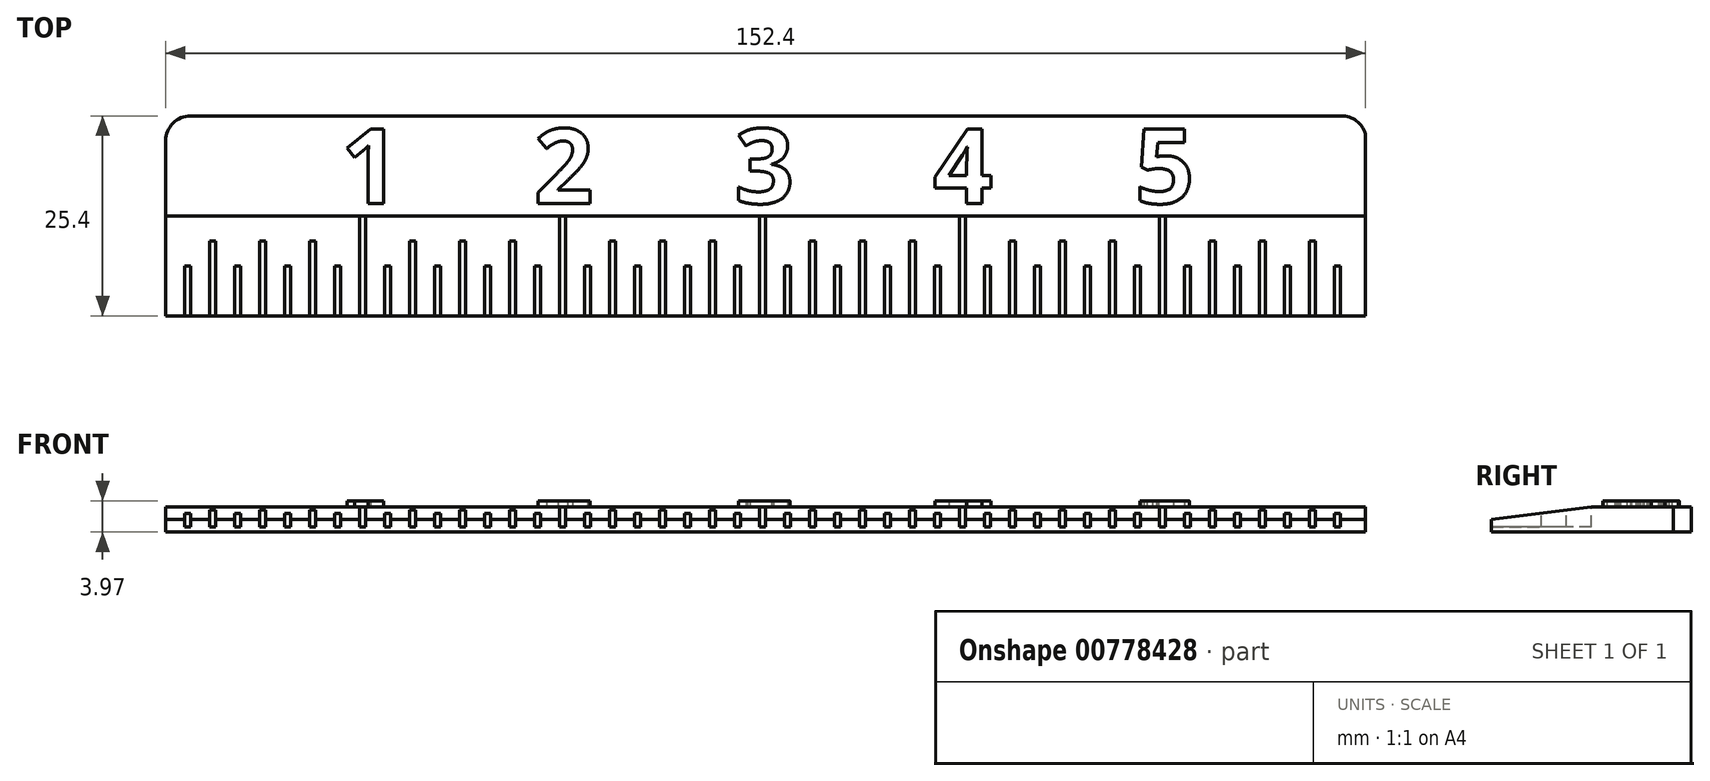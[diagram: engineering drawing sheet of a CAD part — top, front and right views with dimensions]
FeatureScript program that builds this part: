
annotation { "Feature Type Name" : "Feature", "Feature Type Description" : "" }
export const myFeature = defineFeature(function(context is Context, id is Id, definition is map)
    precondition{}
    {
        {
            var Q0;
            Q0=qCreatedBy(makeId("Top.planeOp"),FACE);
            var sketch = newSketch(context, id + "F0", { "sketchPlane" : qUnion([Q0])});
            skLineSegment(sketch, "E0.bottom", {"start": v(-76.26, 7.66) * mm, "end": v(76.14, 7.66) * mm});
            skLineSegment(sketch, "E0.top", {"start": v(-76.26, -17.74) * mm, "end": v(76.14, -17.74) * mm});
            skLineSegment(sketch, "E0.left", {"start": v(-76.26, 7.66) * mm, "end": v(-76.26, -17.74) * mm});
            skLineSegment(sketch, "E0.right", {"start": v(76.14, 7.66) * mm, "end": v(76.14, -17.74) * mm});
            skSolve(sketch);
        }
        {
            var Q0;
            Q0 = qSketchRegion(id + "F0", true);
            extrude(context, id + "F1", {"entities" : qUnion([Q0]), "depth" : 3.17 * mm, "offsetDistance" : 25.4 * mm});
        }
        {
            var Q0;
            Q0=makeQuery(id+"F1.opExtrude","CAP_FACE",FACE,{"disambiguationData":[OSD([sQuery(id+"F0.wireOp",EDGE,"E0.bottom"),sQuery(id+"F0.wireOp",EDGE,"E0.top"),sQuery(id+"F0.wireOp",EDGE,"E0.left"),sQuery(id+"F0.wireOp",EDGE,"E0.right")])],"isStart":false});
            var sketch = newSketch(context, id + "F2", { "sketchPlane" : qUnion([Q0])});
            skPoint(sketch, "E1.firstSnap0", {"position": v(-76.26, -5.04) * mm});
            skLineSegment(sketch, "E1.bottom", {"start": v(-51.66, -5.04) * mm, "end": v(-50.86, -5.04) * mm});
            skLineSegment(sketch, "E1.top", {"start": v(-51.66, -17.74) * mm, "end": v(-50.86, -17.74) * mm});
            skLineSegment(sketch, "E1.left", {"start": v(-51.66, -5.04) * mm, "end": v(-51.66, -17.74) * mm});
            skLineSegment(sketch, "E1.right", {"start": v(-50.86, -5.04) * mm, "end": v(-50.86, -17.74) * mm});
            skLineSegment(sketch, "E2.1.0.0", {"start": v(-26.26, -5.04) * mm, "end": v(-25.46, -5.04) * mm});
            skLineSegment(sketch, "E2.1.0.1", {"start": v(-26.26, -5.04) * mm, "end": v(-26.26, -17.74) * mm});
            skLineSegment(sketch, "E2.1.0.2", {"start": v(-25.46, -5.04) * mm, "end": v(-25.46, -17.74) * mm});
            skLineSegment(sketch, "E2.1.0.3", {"start": v(-26.26, -17.74) * mm, "end": v(-25.46, -17.74) * mm});
            skLineSegment(sketch, "E2.2.0.0", {"start": v(-0.86, -5.04) * mm, "end": v(-0.06, -5.04) * mm});
            skLineSegment(sketch, "E2.2.0.1", {"start": v(-0.86, -5.04) * mm, "end": v(-0.86, -17.74) * mm});
            skLineSegment(sketch, "E2.2.0.2", {"start": v(-0.06, -5.04) * mm, "end": v(-0.06, -17.74) * mm});
            skLineSegment(sketch, "E2.2.0.3", {"start": v(-0.86, -17.74) * mm, "end": v(-0.06, -17.74) * mm});
            skLineSegment(sketch, "E2.3.0.0", {"start": v(24.54, -5.04) * mm, "end": v(25.34, -5.04) * mm});
            skLineSegment(sketch, "E2.3.0.1", {"start": v(24.54, -5.04) * mm, "end": v(24.54, -17.74) * mm});
            skLineSegment(sketch, "E2.3.0.2", {"start": v(25.34, -5.04) * mm, "end": v(25.34, -17.74) * mm});
            skLineSegment(sketch, "E2.3.0.3", {"start": v(24.54, -17.74) * mm, "end": v(25.34, -17.74) * mm});
            skLineSegment(sketch, "E2.4.0.0", {"start": v(49.94, -5.04) * mm, "end": v(50.74, -5.04) * mm});
            skLineSegment(sketch, "E2.4.0.1", {"start": v(49.94, -5.04) * mm, "end": v(49.94, -17.74) * mm});
            skLineSegment(sketch, "E2.4.0.2", {"start": v(50.74, -5.04) * mm, "end": v(50.74, -17.74) * mm});
            skLineSegment(sketch, "E2.4.0.3", {"start": v(49.94, -17.74) * mm, "end": v(50.74, -17.74) * mm});
            skLineSegment(sketch, "E2.direction1", {"start": v(-51.66, -17.74) * mm, "end": v(-26.26, -17.74) * mm, "construction": true});
            skSolve(sketch);
        }
        {
            var Q0;
            Q0 = qSketchRegion(id + "F2", true);
            extrude(context, id + "F3", {"entities" : qUnion([Q0]), "operationType" : NewBodyOperationType.REMOVE, "oppositeDirection" : true, "depth" : 2.54 * mm, "offsetDistance" : 25.4 * mm});
        }
        {
            var Q0;
            Q0=makeQuery(id+"F1.opExtrude","CAP_FACE",FACE,{"disambiguationData":[OSD([sQuery(id+"F0.wireOp",EDGE,"E0.bottom"),sQuery(id+"F0.wireOp",EDGE,"E0.top"),sQuery(id+"F0.wireOp",EDGE,"E0.left"),sQuery(id+"F0.wireOp",EDGE,"E0.right")])],"isStart":false});
            var sketch = newSketch(context, id + "F4", { "sketchPlane" : qUnion([Q0])});
            skLineSegment(sketch, "E3.bottom", {"start": v(-70.7, -8.21) * mm, "end": v(-69.91, -8.21) * mm});
            skLineSegment(sketch, "E3.top", {"start": v(-70.7, -17.74) * mm, "end": v(-69.91, -17.74) * mm});
            skLineSegment(sketch, "E3.left", {"start": v(-70.7, -8.21) * mm, "end": v(-70.7, -17.74) * mm});
            skLineSegment(sketch, "E3.right", {"start": v(-69.91, -8.21) * mm, "end": v(-69.91, -17.74) * mm});
            skLineSegment(sketch, "E4.1.0.0", {"start": v(-64.36, -8.21) * mm, "end": v(-64.36, -17.74) * mm});
            skLineSegment(sketch, "E4.1.0.1", {"start": v(-63.56, -8.21) * mm, "end": v(-63.56, -17.74) * mm});
            skLineSegment(sketch, "E4.1.0.2", {"start": v(-64.36, -8.21) * mm, "end": v(-63.56, -8.21) * mm});
            skLineSegment(sketch, "E4.1.0.3", {"start": v(-64.36, -17.74) * mm, "end": v(-63.56, -17.74) * mm});
            skLineSegment(sketch, "E4.2.0.0", {"start": v(-58, -8.21) * mm, "end": v(-58, -17.74) * mm});
            skLineSegment(sketch, "E4.2.0.1", {"start": v(-57.21, -8.21) * mm, "end": v(-57.21, -17.74) * mm});
            skLineSegment(sketch, "E4.2.0.2", {"start": v(-58, -8.21) * mm, "end": v(-57.21, -8.21) * mm});
            skLineSegment(sketch, "E4.2.0.3", {"start": v(-58, -17.74) * mm, "end": v(-57.21, -17.74) * mm});
            skLineSegment(sketch, "E4.direction1", {"start": v(-70.7, -17.74) * mm, "end": v(-64.36, -17.74) * mm, "construction": true});
            skLineSegment(sketch, "E5.1.0.0", {"start": v(-31.81, -8.21) * mm, "end": v(-31.81, -17.74) * mm});
            skLineSegment(sketch, "E5.1.0.1", {"start": v(-32.6, -17.74) * mm, "end": v(-31.81, -17.74) * mm});
            skLineSegment(sketch, "E5.1.0.2", {"start": v(-45.3, -17.74) * mm, "end": v(-38.96, -17.74) * mm, "construction": true});
            skLineSegment(sketch, "E5.1.0.3", {"start": v(-32.6, -8.21) * mm, "end": v(-32.6, -17.74) * mm});
            skLineSegment(sketch, "E5.1.0.4", {"start": v(-38.96, -17.74) * mm, "end": v(-38.16, -17.74) * mm});
            skLineSegment(sketch, "E5.1.0.5", {"start": v(-38.16, -8.21) * mm, "end": v(-38.16, -17.74) * mm});
            skLineSegment(sketch, "E5.1.0.6", {"start": v(-38.96, -8.21) * mm, "end": v(-38.96, -17.74) * mm});
            skLineSegment(sketch, "E5.1.0.7", {"start": v(-44.51, -8.21) * mm, "end": v(-44.51, -17.74) * mm});
            skLineSegment(sketch, "E5.1.0.8", {"start": v(-45.3, -8.21) * mm, "end": v(-45.3, -17.74) * mm});
            skLineSegment(sketch, "E5.1.0.9", {"start": v(-45.3, -17.74) * mm, "end": v(-44.51, -17.74) * mm});
            skLineSegment(sketch, "E5.1.0.10", {"start": v(-32.6, -8.21) * mm, "end": v(-31.81, -8.21) * mm});
            skLineSegment(sketch, "E5.1.0.11", {"start": v(-38.96, -8.21) * mm, "end": v(-38.16, -8.21) * mm});
            skLineSegment(sketch, "E5.1.0.12", {"start": v(-45.3, -8.21) * mm, "end": v(-44.51, -8.21) * mm});
            skLineSegment(sketch, "E5.2.0.0", {"start": v(-6.41, -8.21) * mm, "end": v(-6.41, -17.74) * mm});
            skLineSegment(sketch, "E5.2.0.1", {"start": v(-7.2, -17.74) * mm, "end": v(-6.41, -17.74) * mm});
            skLineSegment(sketch, "E5.2.0.2", {"start": v(-19.9, -17.74) * mm, "end": v(-13.56, -17.74) * mm, "construction": true});
            skLineSegment(sketch, "E5.2.0.3", {"start": v(-7.2, -8.21) * mm, "end": v(-7.2, -17.74) * mm});
            skLineSegment(sketch, "E5.2.0.4", {"start": v(-13.56, -17.74) * mm, "end": v(-12.76, -17.74) * mm});
            skLineSegment(sketch, "E5.2.0.5", {"start": v(-12.76, -8.21) * mm, "end": v(-12.76, -17.74) * mm});
            skLineSegment(sketch, "E5.2.0.6", {"start": v(-13.56, -8.21) * mm, "end": v(-13.56, -17.74) * mm});
            skLineSegment(sketch, "E5.2.0.7", {"start": v(-19.11, -8.21) * mm, "end": v(-19.11, -17.74) * mm});
            skLineSegment(sketch, "E5.2.0.8", {"start": v(-19.9, -8.21) * mm, "end": v(-19.9, -17.74) * mm});
            skLineSegment(sketch, "E5.2.0.9", {"start": v(-19.9, -17.74) * mm, "end": v(-19.11, -17.74) * mm});
            skLineSegment(sketch, "E5.2.0.10", {"start": v(-7.2, -8.21) * mm, "end": v(-6.41, -8.21) * mm});
            skLineSegment(sketch, "E5.2.0.11", {"start": v(-13.56, -8.21) * mm, "end": v(-12.76, -8.21) * mm});
            skLineSegment(sketch, "E5.2.0.12", {"start": v(-19.9, -8.21) * mm, "end": v(-19.11, -8.21) * mm});
            skLineSegment(sketch, "E5.3.0.0", {"start": v(18.99, -8.21) * mm, "end": v(18.99, -17.74) * mm});
            skLineSegment(sketch, "E5.3.0.1", {"start": v(18.2, -17.74) * mm, "end": v(18.99, -17.74) * mm});
            skLineSegment(sketch, "E5.3.0.2", {"start": v(5.5, -17.74) * mm, "end": v(11.84, -17.74) * mm, "construction": true});
            skLineSegment(sketch, "E5.3.0.3", {"start": v(18.2, -8.21) * mm, "end": v(18.2, -17.74) * mm});
            skLineSegment(sketch, "E5.3.0.4", {"start": v(11.84, -17.74) * mm, "end": v(12.64, -17.74) * mm});
            skLineSegment(sketch, "E5.3.0.5", {"start": v(12.64, -8.21) * mm, "end": v(12.64, -17.74) * mm});
            skLineSegment(sketch, "E5.3.0.6", {"start": v(11.84, -8.21) * mm, "end": v(11.84, -17.74) * mm});
            skLineSegment(sketch, "E5.3.0.7", {"start": v(6.29, -8.21) * mm, "end": v(6.29, -17.74) * mm});
            skLineSegment(sketch, "E5.3.0.8", {"start": v(5.5, -8.21) * mm, "end": v(5.5, -17.74) * mm});
            skLineSegment(sketch, "E5.3.0.9", {"start": v(5.5, -17.74) * mm, "end": v(6.29, -17.74) * mm});
            skLineSegment(sketch, "E5.3.0.10", {"start": v(18.2, -8.21) * mm, "end": v(18.99, -8.21) * mm});
            skLineSegment(sketch, "E5.3.0.11", {"start": v(11.84, -8.21) * mm, "end": v(12.64, -8.21) * mm});
            skLineSegment(sketch, "E5.3.0.12", {"start": v(5.5, -8.21) * mm, "end": v(6.29, -8.21) * mm});
            skLineSegment(sketch, "E5.4.0.0", {"start": v(44.39, -8.21) * mm, "end": v(44.39, -17.74) * mm});
            skLineSegment(sketch, "E5.4.0.1", {"start": v(43.6, -17.74) * mm, "end": v(44.39, -17.74) * mm});
            skLineSegment(sketch, "E5.4.0.2", {"start": v(30.9, -17.74) * mm, "end": v(37.24, -17.74) * mm, "construction": true});
            skLineSegment(sketch, "E5.4.0.3", {"start": v(43.6, -8.21) * mm, "end": v(43.6, -17.74) * mm});
            skLineSegment(sketch, "E5.4.0.4", {"start": v(37.24, -17.74) * mm, "end": v(38.04, -17.74) * mm});
            skLineSegment(sketch, "E5.4.0.5", {"start": v(38.04, -8.21) * mm, "end": v(38.04, -17.74) * mm});
            skLineSegment(sketch, "E5.4.0.6", {"start": v(37.24, -8.21) * mm, "end": v(37.24, -17.74) * mm});
            skLineSegment(sketch, "E5.4.0.7", {"start": v(31.69, -8.21) * mm, "end": v(31.69, -17.74) * mm});
            skLineSegment(sketch, "E5.4.0.8", {"start": v(30.9, -8.21) * mm, "end": v(30.9, -17.74) * mm});
            skLineSegment(sketch, "E5.4.0.9", {"start": v(30.9, -17.74) * mm, "end": v(31.69, -17.74) * mm});
            skLineSegment(sketch, "E5.4.0.10", {"start": v(43.6, -8.21) * mm, "end": v(44.39, -8.21) * mm});
            skLineSegment(sketch, "E5.4.0.11", {"start": v(37.24, -8.21) * mm, "end": v(38.04, -8.21) * mm});
            skLineSegment(sketch, "E5.4.0.12", {"start": v(30.9, -8.21) * mm, "end": v(31.69, -8.21) * mm});
            skLineSegment(sketch, "E5.5.0.0", {"start": v(69.79, -8.21) * mm, "end": v(69.79, -17.74) * mm});
            skLineSegment(sketch, "E5.5.0.1", {"start": v(69, -17.74) * mm, "end": v(69.79, -17.74) * mm});
            skLineSegment(sketch, "E5.5.0.2", {"start": v(56.3, -17.74) * mm, "end": v(62.64, -17.74) * mm, "construction": true});
            skLineSegment(sketch, "E5.5.0.3", {"start": v(69, -8.21) * mm, "end": v(69, -17.74) * mm});
            skLineSegment(sketch, "E5.5.0.4", {"start": v(62.64, -17.74) * mm, "end": v(63.44, -17.74) * mm});
            skLineSegment(sketch, "E5.5.0.5", {"start": v(63.44, -8.21) * mm, "end": v(63.44, -17.74) * mm});
            skLineSegment(sketch, "E5.5.0.6", {"start": v(62.64, -8.21) * mm, "end": v(62.64, -17.74) * mm});
            skLineSegment(sketch, "E5.5.0.7", {"start": v(57.09, -8.21) * mm, "end": v(57.09, -17.74) * mm});
            skLineSegment(sketch, "E5.5.0.8", {"start": v(56.3, -8.21) * mm, "end": v(56.3, -17.74) * mm});
            skLineSegment(sketch, "E5.5.0.9", {"start": v(56.3, -17.74) * mm, "end": v(57.09, -17.74) * mm});
            skLineSegment(sketch, "E5.5.0.10", {"start": v(69, -8.21) * mm, "end": v(69.79, -8.21) * mm});
            skLineSegment(sketch, "E5.5.0.11", {"start": v(62.64, -8.21) * mm, "end": v(63.44, -8.21) * mm});
            skLineSegment(sketch, "E5.5.0.12", {"start": v(56.3, -8.21) * mm, "end": v(57.09, -8.21) * mm});
            skLineSegment(sketch, "E5.direction1", {"start": v(-70.7, -17.74) * mm, "end": v(-45.3, -17.74) * mm, "construction": true});
            skSolve(sketch);
        }
        {
            var Q0;
            Q0 = qSketchRegion(id + "F4", true);
            extrude(context, id + "F5", {"entities" : qUnion([Q0]), "operationType" : NewBodyOperationType.REMOVE, "oppositeDirection" : true, "depth" : 2.54 * mm, "offsetDistance" : 25.4 * mm});
        }
        {
            var Q0;
            Q0=makeQuery(id+"F1.opExtrude","CAP_FACE",FACE,{"disambiguationData":[OSD([sQuery(id+"F0.wireOp",EDGE,"E0.bottom"),sQuery(id+"F0.wireOp",EDGE,"E0.top"),sQuery(id+"F0.wireOp",EDGE,"E0.left"),sQuery(id+"F0.wireOp",EDGE,"E0.right")])],"isStart":false});
            var sketch = newSketch(context, id + "F6", { "sketchPlane" : qUnion([Q0])});
            skLineSegment(sketch, "E6.bottom", {"start": v(-73.88, -17.74) * mm, "end": v(-73.09, -17.74) * mm});
            skLineSegment(sketch, "E6.top", {"start": v(-73.88, -11.39) * mm, "end": v(-73.09, -11.39) * mm});
            skLineSegment(sketch, "E6.left", {"start": v(-73.88, -17.74) * mm, "end": v(-73.88, -11.39) * mm});
            skLineSegment(sketch, "E6.right", {"start": v(-73.09, -17.74) * mm, "end": v(-73.09, -11.39) * mm});
            skLineSegment(sketch, "E7.1.0.0", {"start": v(-67.53, -17.74) * mm, "end": v(-66.74, -17.74) * mm});
            skLineSegment(sketch, "E7.1.0.1", {"start": v(-67.53, -11.39) * mm, "end": v(-66.74, -11.39) * mm});
            skLineSegment(sketch, "E7.1.0.2", {"start": v(-67.53, -17.74) * mm, "end": v(-67.53, -11.39) * mm});
            skLineSegment(sketch, "E7.1.0.3", {"start": v(-66.74, -17.74) * mm, "end": v(-66.74, -11.39) * mm});
            skLineSegment(sketch, "E7.2.0.0", {"start": v(-61.18, -17.74) * mm, "end": v(-60.39, -17.74) * mm});
            skLineSegment(sketch, "E7.2.0.1", {"start": v(-61.18, -11.39) * mm, "end": v(-60.39, -11.39) * mm});
            skLineSegment(sketch, "E7.2.0.2", {"start": v(-61.18, -17.74) * mm, "end": v(-61.18, -11.39) * mm});
            skLineSegment(sketch, "E7.2.0.3", {"start": v(-60.39, -17.74) * mm, "end": v(-60.39, -11.39) * mm});
            skLineSegment(sketch, "E7.3.0.0", {"start": v(-54.83, -17.74) * mm, "end": v(-54.04, -17.74) * mm});
            skLineSegment(sketch, "E7.3.0.1", {"start": v(-54.83, -11.39) * mm, "end": v(-54.04, -11.39) * mm});
            skLineSegment(sketch, "E7.3.0.2", {"start": v(-54.83, -17.74) * mm, "end": v(-54.83, -11.39) * mm});
            skLineSegment(sketch, "E7.3.0.3", {"start": v(-54.04, -17.74) * mm, "end": v(-54.04, -11.39) * mm});
            skLineSegment(sketch, "E7.direction1", {"start": v(-73.88, -17.74) * mm, "end": v(-67.53, -17.74) * mm, "construction": true});
            skLineSegment(sketch, "E8.1.0.0", {"start": v(-29.43, -17.74) * mm, "end": v(-28.64, -17.74) * mm});
            skLineSegment(sketch, "E8.1.0.1", {"start": v(-34.99, -17.74) * mm, "end": v(-34.99, -11.39) * mm});
            skLineSegment(sketch, "E8.1.0.2", {"start": v(-35.78, -17.74) * mm, "end": v(-35.78, -11.39) * mm});
            skLineSegment(sketch, "E8.1.0.3", {"start": v(-48.48, -17.74) * mm, "end": v(-42.13, -17.74) * mm, "construction": true});
            skLineSegment(sketch, "E8.1.0.4", {"start": v(-35.78, -11.39) * mm, "end": v(-34.99, -11.39) * mm});
            skLineSegment(sketch, "E8.1.0.5", {"start": v(-35.78, -17.74) * mm, "end": v(-34.99, -17.74) * mm});
            skLineSegment(sketch, "E8.1.0.6", {"start": v(-29.43, -11.39) * mm, "end": v(-28.64, -11.39) * mm});
            skLineSegment(sketch, "E8.1.0.7", {"start": v(-29.43, -17.74) * mm, "end": v(-29.43, -11.39) * mm});
            skLineSegment(sketch, "E8.1.0.8", {"start": v(-28.64, -17.74) * mm, "end": v(-28.64, -11.39) * mm});
            skLineSegment(sketch, "E8.1.0.9", {"start": v(-48.48, -11.39) * mm, "end": v(-47.69, -11.39) * mm});
            skLineSegment(sketch, "E8.1.0.10", {"start": v(-48.48, -17.74) * mm, "end": v(-48.48, -11.39) * mm});
            skLineSegment(sketch, "E8.1.0.11", {"start": v(-47.69, -17.74) * mm, "end": v(-47.69, -11.39) * mm});
            skLineSegment(sketch, "E8.1.0.12", {"start": v(-42.13, -17.74) * mm, "end": v(-41.34, -17.74) * mm});
            skLineSegment(sketch, "E8.1.0.13", {"start": v(-42.13, -11.39) * mm, "end": v(-41.34, -11.39) * mm});
            skLineSegment(sketch, "E8.1.0.14", {"start": v(-42.13, -17.74) * mm, "end": v(-42.13, -11.39) * mm});
            skLineSegment(sketch, "E8.1.0.15", {"start": v(-41.34, -17.74) * mm, "end": v(-41.34, -11.39) * mm});
            skLineSegment(sketch, "E8.1.0.16", {"start": v(-48.48, -17.74) * mm, "end": v(-47.69, -17.74) * mm});
            skLineSegment(sketch, "E8.2.0.0", {"start": v(-4.03, -17.74) * mm, "end": v(-3.24, -17.74) * mm});
            skLineSegment(sketch, "E8.2.0.1", {"start": v(-9.59, -17.74) * mm, "end": v(-9.59, -11.39) * mm});
            skLineSegment(sketch, "E8.2.0.2", {"start": v(-10.38, -17.74) * mm, "end": v(-10.38, -11.39) * mm});
            skLineSegment(sketch, "E8.2.0.3", {"start": v(-23.08, -17.74) * mm, "end": v(-16.73, -17.74) * mm, "construction": true});
            skLineSegment(sketch, "E8.2.0.4", {"start": v(-10.38, -11.39) * mm, "end": v(-9.59, -11.39) * mm});
            skLineSegment(sketch, "E8.2.0.5", {"start": v(-10.38, -17.74) * mm, "end": v(-9.59, -17.74) * mm});
            skLineSegment(sketch, "E8.2.0.6", {"start": v(-4.03, -11.39) * mm, "end": v(-3.24, -11.39) * mm});
            skLineSegment(sketch, "E8.2.0.7", {"start": v(-4.03, -17.74) * mm, "end": v(-4.03, -11.39) * mm});
            skLineSegment(sketch, "E8.2.0.8", {"start": v(-3.24, -17.74) * mm, "end": v(-3.24, -11.39) * mm});
            skLineSegment(sketch, "E8.2.0.9", {"start": v(-23.08, -11.39) * mm, "end": v(-22.29, -11.39) * mm});
            skLineSegment(sketch, "E8.2.0.10", {"start": v(-23.08, -17.74) * mm, "end": v(-23.08, -11.39) * mm});
            skLineSegment(sketch, "E8.2.0.11", {"start": v(-22.29, -17.74) * mm, "end": v(-22.29, -11.39) * mm});
            skLineSegment(sketch, "E8.2.0.12", {"start": v(-16.73, -17.74) * mm, "end": v(-15.94, -17.74) * mm});
            skLineSegment(sketch, "E8.2.0.13", {"start": v(-16.73, -11.39) * mm, "end": v(-15.94, -11.39) * mm});
            skLineSegment(sketch, "E8.2.0.14", {"start": v(-16.73, -17.74) * mm, "end": v(-16.73, -11.39) * mm});
            skLineSegment(sketch, "E8.2.0.15", {"start": v(-15.94, -17.74) * mm, "end": v(-15.94, -11.39) * mm});
            skLineSegment(sketch, "E8.2.0.16", {"start": v(-23.08, -17.74) * mm, "end": v(-22.29, -17.74) * mm});
            skLineSegment(sketch, "E8.3.0.0", {"start": v(21.37, -17.74) * mm, "end": v(22.16, -17.74) * mm});
            skLineSegment(sketch, "E8.3.0.1", {"start": v(15.81, -17.74) * mm, "end": v(15.81, -11.39) * mm});
            skLineSegment(sketch, "E8.3.0.2", {"start": v(15.02, -17.74) * mm, "end": v(15.02, -11.39) * mm});
            skLineSegment(sketch, "E8.3.0.3", {"start": v(2.32, -17.74) * mm, "end": v(8.67, -17.74) * mm, "construction": true});
            skLineSegment(sketch, "E8.3.0.4", {"start": v(15.02, -11.39) * mm, "end": v(15.81, -11.39) * mm});
            skLineSegment(sketch, "E8.3.0.5", {"start": v(15.02, -17.74) * mm, "end": v(15.81, -17.74) * mm});
            skLineSegment(sketch, "E8.3.0.6", {"start": v(21.37, -11.39) * mm, "end": v(22.16, -11.39) * mm});
            skLineSegment(sketch, "E8.3.0.7", {"start": v(21.37, -17.74) * mm, "end": v(21.37, -11.39) * mm});
            skLineSegment(sketch, "E8.3.0.8", {"start": v(22.16, -17.74) * mm, "end": v(22.16, -11.39) * mm});
            skLineSegment(sketch, "E8.3.0.9", {"start": v(2.32, -11.39) * mm, "end": v(3.11, -11.39) * mm});
            skLineSegment(sketch, "E8.3.0.10", {"start": v(2.32, -17.74) * mm, "end": v(2.32, -11.39) * mm});
            skLineSegment(sketch, "E8.3.0.11", {"start": v(3.11, -17.74) * mm, "end": v(3.11, -11.39) * mm});
            skLineSegment(sketch, "E8.3.0.12", {"start": v(8.67, -17.74) * mm, "end": v(9.46, -17.74) * mm});
            skLineSegment(sketch, "E8.3.0.13", {"start": v(8.67, -11.39) * mm, "end": v(9.46, -11.39) * mm});
            skLineSegment(sketch, "E8.3.0.14", {"start": v(8.67, -17.74) * mm, "end": v(8.67, -11.39) * mm});
            skLineSegment(sketch, "E8.3.0.15", {"start": v(9.46, -17.74) * mm, "end": v(9.46, -11.39) * mm});
            skLineSegment(sketch, "E8.3.0.16", {"start": v(2.32, -17.74) * mm, "end": v(3.11, -17.74) * mm});
            skLineSegment(sketch, "E8.4.0.0", {"start": v(46.77, -17.74) * mm, "end": v(47.56, -17.74) * mm});
            skLineSegment(sketch, "E8.4.0.1", {"start": v(41.21, -17.74) * mm, "end": v(41.21, -11.39) * mm});
            skLineSegment(sketch, "E8.4.0.2", {"start": v(40.42, -17.74) * mm, "end": v(40.42, -11.39) * mm});
            skLineSegment(sketch, "E8.4.0.3", {"start": v(27.72, -17.74) * mm, "end": v(34.07, -17.74) * mm, "construction": true});
            skLineSegment(sketch, "E8.4.0.4", {"start": v(40.42, -11.39) * mm, "end": v(41.21, -11.39) * mm});
            skLineSegment(sketch, "E8.4.0.5", {"start": v(40.42, -17.74) * mm, "end": v(41.21, -17.74) * mm});
            skLineSegment(sketch, "E8.4.0.6", {"start": v(46.77, -11.39) * mm, "end": v(47.56, -11.39) * mm});
            skLineSegment(sketch, "E8.4.0.7", {"start": v(46.77, -17.74) * mm, "end": v(46.77, -11.39) * mm});
            skLineSegment(sketch, "E8.4.0.8", {"start": v(47.56, -17.74) * mm, "end": v(47.56, -11.39) * mm});
            skLineSegment(sketch, "E8.4.0.9", {"start": v(27.72, -11.39) * mm, "end": v(28.51, -11.39) * mm});
            skLineSegment(sketch, "E8.4.0.10", {"start": v(27.72, -17.74) * mm, "end": v(27.72, -11.39) * mm});
            skLineSegment(sketch, "E8.4.0.11", {"start": v(28.51, -17.74) * mm, "end": v(28.51, -11.39) * mm});
            skLineSegment(sketch, "E8.4.0.12", {"start": v(34.07, -17.74) * mm, "end": v(34.86, -17.74) * mm});
            skLineSegment(sketch, "E8.4.0.13", {"start": v(34.07, -11.39) * mm, "end": v(34.86, -11.39) * mm});
            skLineSegment(sketch, "E8.4.0.14", {"start": v(34.07, -17.74) * mm, "end": v(34.07, -11.39) * mm});
            skLineSegment(sketch, "E8.4.0.15", {"start": v(34.86, -17.74) * mm, "end": v(34.86, -11.39) * mm});
            skLineSegment(sketch, "E8.4.0.16", {"start": v(27.72, -17.74) * mm, "end": v(28.51, -17.74) * mm});
            skLineSegment(sketch, "E8.5.0.0", {"start": v(72.17, -17.74) * mm, "end": v(72.96, -17.74) * mm});
            skLineSegment(sketch, "E8.5.0.1", {"start": v(66.61, -17.74) * mm, "end": v(66.61, -11.39) * mm});
            skLineSegment(sketch, "E8.5.0.2", {"start": v(65.82, -17.74) * mm, "end": v(65.82, -11.39) * mm});
            skLineSegment(sketch, "E8.5.0.3", {"start": v(53.12, -17.74) * mm, "end": v(59.47, -17.74) * mm, "construction": true});
            skLineSegment(sketch, "E8.5.0.4", {"start": v(65.82, -11.39) * mm, "end": v(66.61, -11.39) * mm});
            skLineSegment(sketch, "E8.5.0.5", {"start": v(65.82, -17.74) * mm, "end": v(66.61, -17.74) * mm});
            skLineSegment(sketch, "E8.5.0.6", {"start": v(72.17, -11.39) * mm, "end": v(72.96, -11.39) * mm});
            skLineSegment(sketch, "E8.5.0.7", {"start": v(72.17, -17.74) * mm, "end": v(72.17, -11.39) * mm});
            skLineSegment(sketch, "E8.5.0.8", {"start": v(72.96, -17.74) * mm, "end": v(72.96, -11.39) * mm});
            skLineSegment(sketch, "E8.5.0.9", {"start": v(53.12, -11.39) * mm, "end": v(53.91, -11.39) * mm});
            skLineSegment(sketch, "E8.5.0.10", {"start": v(53.12, -17.74) * mm, "end": v(53.12, -11.39) * mm});
            skLineSegment(sketch, "E8.5.0.11", {"start": v(53.91, -17.74) * mm, "end": v(53.91, -11.39) * mm});
            skLineSegment(sketch, "E8.5.0.12", {"start": v(59.47, -17.74) * mm, "end": v(60.26, -17.74) * mm});
            skLineSegment(sketch, "E8.5.0.13", {"start": v(59.47, -11.39) * mm, "end": v(60.26, -11.39) * mm});
            skLineSegment(sketch, "E8.5.0.14", {"start": v(59.47, -17.74) * mm, "end": v(59.47, -11.39) * mm});
            skLineSegment(sketch, "E8.5.0.15", {"start": v(60.26, -17.74) * mm, "end": v(60.26, -11.39) * mm});
            skLineSegment(sketch, "E8.5.0.16", {"start": v(53.12, -17.74) * mm, "end": v(53.91, -17.74) * mm});
            skLineSegment(sketch, "E8.direction1", {"start": v(-73.88, -17.74) * mm, "end": v(-48.48, -17.74) * mm, "construction": true});
            skSolve(sketch);
        }
        {
            var Q0;
            Q0 = qSketchRegion(id + "F6", true);
            extrude(context, id + "F7", {"entities" : qUnion([Q0]), "operationType" : NewBodyOperationType.REMOVE, "oppositeDirection" : true, "depth" : 2.54 * mm, "offsetDistance" : 25.4 * mm});
        }
        {
            var Q0;
            Q0=makeQuery(id+"F1.opExtrude","CAP_FACE",FACE,{"disambiguationData":[OSD([sQuery(id+"F0.wireOp",EDGE,"E0.bottom"),sQuery(id+"F0.wireOp",EDGE,"E0.top"),sQuery(id+"F0.wireOp",EDGE,"E0.left"),sQuery(id+"F0.wireOp",EDGE,"E0.right")])],"isStart":false});
            var sketch = newSketch(context, id + "F8", { "sketchPlane" : qUnion([Q0])});
            skLineSegment(sketch, "E9", {"start": v(-76.26, 6.08) * mm, "end": v(76.14, 6.08) * mm, "construction": true});
            skLineSegment(sketch, "E10", {"start": v(76.14, 6.08) * mm, "end": v(76.14, -3.45) * mm, "construction": true});
            skLineSegment(sketch, "E11", {"start": v(76.14, -3.45) * mm, "end": v(-76.26, -3.45) * mm, "construction": true});
            skText(sketch, "E12", { "text": "1", "fontName": "OpenSans-Bold.ttf"});
            skText(sketch, "E13", { "text": "2", "fontName": "OpenSans-Bold.ttf"});
            skText(sketch, "E14", { "text": "3", "fontName": "OpenSans-Bold.ttf"});
            skText(sketch, "E15", { "text": "4", "fontName": "OpenSans-Bold.ttf"});
            skText(sketch, "E16", { "text": "5", "fontName": "OpenSans-Bold.ttf"});
            const initialGuessF8  = {"E12": [-0.05402, -0.00345, 1, 0, 0.00952], "E13": [-0.02946, -0.00345, 1, 0, 0.00953], "E14": [-0.00401, -0.00345, 1, 0, 0.00953], "E15": [0.02124, -0.00345, 1, 0, 0.00952], "E16": [0.04683, -0.00345, 1, 0, 0.00952]};
            skSetInitialGuess(sketch, initialGuessF8);
            skSolve(sketch);
        }
        {
            var Q0;
            Q0 = qSketchRegion(id + "F8", true);
            extrude(context, id + "F9", {"entities" : qUnion([Q0]), "operationType" : NewBodyOperationType.ADD, "depth" : 0.8 * mm, "offsetDistance" : 25.4 * mm});
        }
        {
            var Q0;
            Q0=makeQuery(id+"F1.opExtrude","SWEPT_FACE",FACE,{"disambiguationData":[OSD([sQuery(id+"F0.wireOp",EDGE,"E0.right")])]});
            var sketch = newSketch(context, id + "F10", { "sketchPlane" : qUnion([Q0])});
            skLineSegment(sketch, "E17", {"start": v(-17.74, 1.59) * mm, "end": v(-5.04, 3.18) * mm});
            skLineSegment(sketch, "E18", {"start": v(-5.04, 3.18) * mm, "end": v(-17.74, 3.18) * mm});
            skLineSegment(sketch, "E19", {"start": v(-17.74, 3.18) * mm, "end": v(-17.74, 1.59) * mm});
            skSolve(sketch);
        }
        {
            var Q0;
            Q0 = qSketchRegion(id + "F10", true);
            extrude(context, id + "F11", {"entities" : qUnion([Q0]), "operationType" : NewBodyOperationType.REMOVE, "endBound" : BoundingType.THROUGH_ALL, "oppositeDirection" : true, "depth" : 25.4 * mm, "offsetDistance" : 25.4 * mm});
        }
        {
            var Q0;
            {var subQ0=sQuery(id+"F0.wireOp",EDGE,"E0.bottom");var subQ1=sQuery(id+"F0.wireOp",EDGE,"E0.right");var subQ2=sQuery(id+"F0.wireOp",EDGE,"E0.top");var subQ3=sQuery(id+"F0.wireOp",EDGE,"E0.left");Q0=makeQuery(id+"F9.boolean.opBoolean","SPLIT",FACE,{"disambiguationData":[TD([makeQuery(id+"F1.opExtrude","SWEPT_FACE",FACE,{"disambiguationData":[OSD([subQ0])]})])],"derivedFrom":makeQuery(id+"F1.opExtrude","CAP_FACE",FACE,{"disambiguationData":[OSD([subQ0,subQ2,subQ3,subQ1])],"isStart":false})});}
            var sketch = newSketch(context, id + "F12", { "sketchPlane" : qUnion([Q0])});
            skArc(sketch, "E20", {"start": v(-73.09, 7.66) * mm, "mid": v(-75.33, 6.73) * mm, "end": v(-76.26, 4.49) * mm});
            skLineSegment(sketch, "E21", {"start": v(-76.26, 4.49) * mm, "end": v(-76.26, 7.66) * mm});
            skLineSegment(sketch, "E22", {"start": v(-76.26, 7.66) * mm, "end": v(-73.09, 7.66) * mm});
            skLineSegment(sketch, "E23.MirrorCS", {"start": v(76.26, 4.49) * mm, "end": v(76.26, 7.66) * mm});
            skArc(sketch, "E24.MirrorCS", {"start": v(73.09, 7.66) * mm, "mid": v(75.33, 6.73) * mm, "end": v(76.26, 4.49) * mm});
            skLineSegment(sketch, "E25.MirrorCS", {"start": v(76.26, 7.66) * mm, "end": v(73.09, 7.66) * mm});
            skSolve(sketch);
        }
        {
            var Q0;
            Q0 = qSketchRegion(id + "F12", true);
            extrude(context, id + "F13", {"entities" : qUnion([Q0]), "operationType" : NewBodyOperationType.REMOVE, "oppositeDirection" : true, "depth" : 25.4 * mm, "offsetDistance" : 25.4 * mm});
        }
    });
